# Revit family: NBS_DudleyIndustriesLimited_TltPprDpnsrs_RecessedIn-cubicleToiletRollHolderBrushWasteBin
name_source: partatom
category: Specialty Equipment
units: mm (PartAtom-declared; Revit-internal decimal feet)

## family parameters
Cut with Voids When Loaded = Yes
Host = Face
Maintain Annotation Orientation = No
Part Type = Normal
Room Calculation Point = No
Round Connector Dimension = Use Diameter
Shared = No

## types (1)
- RecessedIn-cubicleToiletRollHolderBrushWasteBin
    AssetType = Fixed
    BIMObjectName = NBS_DudleyIndustriesLimited_ToiletPaperDispensers_RecessedIn-cubicleToiletRollHolderBrushWasteBin
    Category = Pr_40_70_22_90:Toilet paper dispensers
    ClearanceZoneMaterial = NBS_ClearanceZone
    CubicleLength = 575 mm
    CubicleMaterial = NBS_DudleyIndustriesLimited_StainlessSteelBrushed
    CubicleWidth = 400 mm  [stored 1.31234 ft]
    Default Elevation = 1219 mm
    Description = A complete cubicle recessed unit.
    DurationUnit = year
    Finish = Brushed,Powder-coated
    Form = Recessed in-cubicle toilet roll holder, brush and waste bin
    IfcExportAs = IfcFurnitureType
    IfcExportType = NOTDEFINED
    InsetDepth = 30 mm  [stored 0.0984252 ft]
    IntegralAccessories = Four fixing clamps
    ManufacturerName = Dudley Industries Limited
    ManufacturerURL = https://www.dudleyindustries.com
    Material = Stainless steel
    MaterialsBody = Stainless steel
    MaterialsFinishAndColour = Brushed stainless steel,Powder coated black
    ModelReference = Recessed In-cubicle Toilet Roll Holder | Brush | Waste Bin
    NBSInstanceId = 9ede9982-3cee-472c-8cd2-b83719dc3938
    NBSObjectId = 002032e9-6f14-4ea2-afd9-6958024e6fc7
    NBSVariantId = 00000000-0000-0000-0000-000000000000
    Name = ToiletPaperDispensers_RecessedIn-cubicleToiletRollHolderBrushWasteBin_DudleyIndustriesLimited
    NominalHeight = 0 mm  [stored 0 ft]
    NominalLength = 0 mm  [stored 0 ft]
    NominalWidth = 0 mm  [stored 0 ft]
    Operation = Pull-out
    ProductInformation = https://source.thenbs.com
    Shape = Rectangle
    Uniclass2015Code = Pr_40_70_22_90
    Uniclass2015Title = Toilet paper dispensers
    Uniclass2015Version = Products v1.37
    Version = 2
    WarrantyDescription = Ten year
    WarrantyDurationUnit = year

note: [stored X ft] marks values corroborated as IEEE doubles in the binary element streams (Revit-internal decimal feet)

## geometry (parser evidence)
native form markers: Sweep x2
no freeform markers — native parametric forms only
